FCSTD DOCUMENT  (FreeCAD 0.19R0.19.2)
Label: 003
License: All rights reserved
LicenseURL: http://en.wikipedia.org/wiki/All_rights_reserved
objects: Sketcher::SketchObject×1
note: 1 computed .brp shape members not serialized (recipe doc carries the construction recipe); baked Part::Feature solids carry a one-line shape summary decoded from their .brp

FEATURE [Sketcher::SketchObject] Sketch
  FullyConstrained = false
  sketch-geometry (14):
    g0: LineSegment StartX=0 StartY=0 StartZ=0 EndX=12.5 EndY=0 EndZ=0
    g1: Circle CenterX=0 CenterY=0 CenterZ=0 NormalX=0 NormalY=0 NormalZ=1 AngleXU=0 Radius=12.5
    g2: LineSegment StartX=0 StartY=0 StartZ=0 EndX=-0.8 EndY=0 EndZ=0
    g3: Circle CenterX=0 CenterY=0 CenterZ=0 NormalX=0 NormalY=0 NormalZ=1 AngleXU=0 Radius=0.8
    g4: LineSegment StartX=0 StartY=0 StartZ=0 EndX=-6.6 EndY=0 EndZ=0
    g5: LineSegment StartX=0 StartY=0 StartZ=0 EndX=6.6 EndY=0 EndZ=0
    g6: LineSegment StartX=0 StartY=0 StartZ=0 EndX=0 EndY=6.7 EndZ=0
    g7: LineSegment StartX=0 StartY=0 StartZ=0 EndX=0 EndY=-6.6 EndZ=0
    g8: LineSegment StartX=0 StartY=6.7 StartZ=0 EndX=0 EndY=10.6 EndZ=0
    g9: Circle CenterX=0 CenterY=6.7 CenterZ=0 NormalX=0 NormalY=0 NormalZ=1 AngleXU=0 Radius=3.9
    g10: Circle CenterX=6.6 CenterY=0 CenterZ=0 NormalX=0 NormalY=0 NormalZ=1 AngleXU=0 Radius=3.9
    g11: Circle CenterX=-6.6 CenterY=0 CenterZ=0 NormalX=0 NormalY=0 NormalZ=1 AngleXU=0 Radius=3.9
    g12: Circle CenterX=0 CenterY=-6.6 CenterZ=0 NormalX=0 NormalY=0 NormalZ=1 AngleXU=0 Radius=3.9
    g13: LineSegment StartX=0 StartY=0 StartZ=0 EndX=6.86782 EndY=6.86782 EndZ=0
  constraints (32):
    c: Horizontal(g0)
    c: Distance(g0) = 12.5
    c: Coincident(g0,g-1)
    c: Coincident(g1,g0)
    c: PointOnObject(g0,g1)
    c: Horizontal(g2)
    c: Distance(g2) = 0.8
    c: Coincident(g2,g0)
    c: Coincident(g3,g0)
    c: PointOnObject(g2,g3)
    c: Coincident(g4,g0)
    c: Distance(g4) = 6.6
    c: Horizontal(g5)
    c: Distance(g5) = 6.6
    c: Coincident(g5,g0)
    c: Vertical(g6)
    c: Distance(g6) = 6.7
    c: Coincident(g6,g0)
    c: Vertical(g7)
    c: Distance(g7) = 6.6
    c: Coincident(g7,g0)
    c: Horizontal(g4)
    c: Vertical(g8)
    c: Distance(g8) = 3.9
    c: Coincident(g8,g6)
    c: Coincident(g9,g6)
    c: PointOnObject(g8,g9)
    c: Coincident(g10,g5)
    c: Coincident(g11,g4)
    c: Coincident(g12,g7)
    c: Coincident(g13,g0)
    c: Angle(g0,g13) = 0.785398
